# Revit family: P710018-031
name_source: partatom
category: Lighting Fixtures
revit_build: Autodesk Revit 2014 (Build: 20130308_1515(x64)
units: mm (PartAtom-declared; Revit-internal decimal feet)

## types (1)
- P710018-031
    Apparent Load = 40 VA
    Assembly Code = D5020200
    Color Filter = 16777215
    Connector Description = Lighting Connector
    Default Elevation = 48 "
    Description = Inspired at its roots by an understated beauty and a breathtaking formal elegance, this wall sconce will make a stunning addition to any luxurious living space. A black arm flows down from an ornamental light base to a rectangular backplate. On top of the light base sits a summer linen shade.
    Diameter = 4.5 "
    Dimming Lamp Color Temperature Shift = <None>
    Fabric = Paint - Hubbell - White Texture
    Features = Inspired at its roots by an understated beauty and a breathtaking formal elegance, this wall sconce will make a stunning addition to any luxurious living space.
A black arm flows down from an ornamental light base to a rectangular backplate.
On top of the light base sits a summer linen shade.
Ideal for any bedroom, living room, sitting room, hallway, or foyer.
Perfect for transitional, modern, farmhouse, contemporary, or luxury settings.
Measures 4-1/2-inch width by 17.13-inch height.
Uses one candelabra base bulb that is sold separately (40w max - LED or incandescent).
Able to be fully dimmable with dimmable bulbs.
Includes installation instructions and mounting hardware.
Progress Lighting products are designed for exceptional quality, reliability, and functionality.
    Fixture distribution = Direct
    Glass = Paint - Hubbell - White Texture
    Gold = Hubbell - Gold
    Height = 6.5 "
    Housing Material = Paint - Hubbell - Textured Camera Black
    Lamp = LED or Incandescent
    Load Classification = Lighting
    Manufacturer = Progress Lighting
    Model = P710018-031
    Photometric Web File = generic.ies
    Power Factor = 1
    Product Documentation Link = https://hubbellcdn.com
    Product Link = https://www.hubbell.com
    Tilt Angle = -90.00°
    URL = https://www.hubbell.com
    Voltage = 120 V
    Warranty = 5 years Warranty
    Wattage Comments = 40W
    Watts = 40 W
    Wood = Wood Planks

## geometry (parser evidence)
native form markers: Sweep x4
no freeform markers — native parametric forms only
